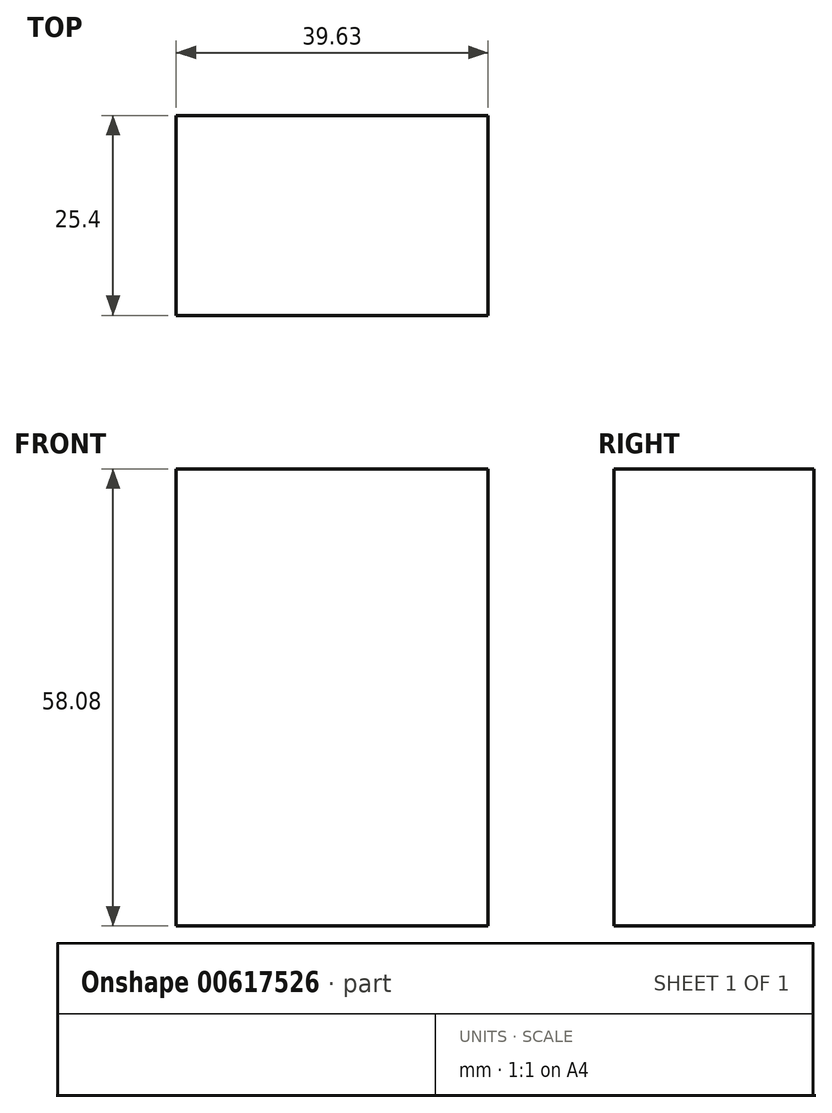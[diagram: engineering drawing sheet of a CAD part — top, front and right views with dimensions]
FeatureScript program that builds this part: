
annotation { "Feature Type Name" : "Feature", "Feature Type Description" : "" }
export const myFeature = defineFeature(function(context is Context, id is Id, definition is map)
    precondition{}
    {
        {
            var Q0;
            Q0=qCreatedBy(makeId("Front.planeOp"),FACE);
            var sketch = newSketch(context, id + "F0", { "sketchPlane" : qUnion([Q0])});
            skLineSegment(sketch, "E0", {"start": v(0, 0) * mm, "end": v(-39.63, 0) * mm});
            skLineSegment(sketch, "E1", {"start": v(-39.63, 0) * mm, "end": v(-39.63, 58.08) * mm});
            skLineSegment(sketch, "E2", {"start": v(-39.63, 58.08) * mm, "end": v(0, 58.08) * mm});
            skLineSegment(sketch, "E3", {"start": v(0, 58.08) * mm, "end": v(0, 0) * mm});
            skLineSegment(sketch, "E4", {"start": v(44.06, -21.4) * mm, "end": v(44.06, -70.36) * mm});
            skLineSegment(sketch, "E5", {"start": v(44.06, -70.36) * mm, "end": v(67, -70.36) * mm});
            skLineSegment(sketch, "E6", {"start": v(44.06, -21.4) * mm, "end": v(62.81, -21.4) * mm});
            skLineSegment(sketch, "E7", {"start": v(62.81, -21.4) * mm, "end": v(62.81, -70.36) * mm});
            skSolve(sketch);
        }
        {
            var Q0;
            Q0 = qSketchRegion(id + "F0", true);
            extrude(context, id + "F1", {"entities" : qUnion([Q0]), "depth" : 25.4 * mm, "offsetDistance" : 25.4 * mm});
        }
        {
            var Q0;
            Q0=makeQuery(id+"F1.opExtrude","SWEPT_BODY",BODY,{"disambiguationData":[OSD([sQuery(id+"F0.wireOp",EDGE,"E4"),sQuery(id+"F0.wireOp",EDGE,"E5"),sQuery(id+"F0.wireOp",EDGE,"E6"),sQuery(id+"F0.wireOp",EDGE,"E7")])]});
            deleteBodies(context, id + "F2", {"entities" : qUnion([Q0])});
        }
    });
